# Revit family: SanitaryComboUnit_Metlam_Compact-2-in-1
name_source: partatom
category: Generic Models
revit_build: Autodesk Revit Architecture 2013 (Build: 20120221_2030(x64)
units: mm (PartAtom-declared; Revit-internal decimal feet)

## types (2) — shared parameters
Assembly Code = E1090900
Depth = 112 mm  [stored 0.367454 ft]
Description = Paper Towel Dispenser & Waste
FilterObject_ANZRS = Sanitary Combination Unit
Height = 720 mm  [stored 2.3622 ft]
Keywords = DISPENSES 350 C-fold paper towels or 475 Multi-fold paper towels. DISPOSAL 6.5L removable S.S. waste container.
Manufacturer = Metlam
Material = Stainless Steel, Satin
ModifiedIssue_ANZRS = 130318.01 $
StyleOrType_ANZRS = Sanitary Ware
Surround Depth = 97 mm  [stored 0.318241 ft]
URL = http://www.metlam.com.au
Width = 365 mm  [stored 1.19751 ft]
zero-valued in all types: Default Elevation

## per-type parameters (varying)
| type | Model | Position - Recessed/Suface Mounted | Product Code | Surround | Void Depth |
| Metlam Sanitary - Compact Paper/Waste Recessed | Compact Paper/Waste - Recessed | 15 mm  [stored 0.0492126 ft] | ML 710 | No | -105 mm  [stored -0.344488 ft] |
| Metlam Sanitary - Compact Paper/Waste Surface Mounted | Compact Paper/Waste - Surface Mounted | 112 mm  [stored 0.367454 ft] | ML 710 SM | Yes | -2 mm  [stored -0.00656168 ft] |

note: [stored X ft] marks values corroborated as IEEE doubles in the binary element streams (Revit-internal decimal feet)

## geometry (parser evidence)
native form markers: Blend x28, Extrusion x1, Sweep x1
no freeform markers — native parametric forms only
